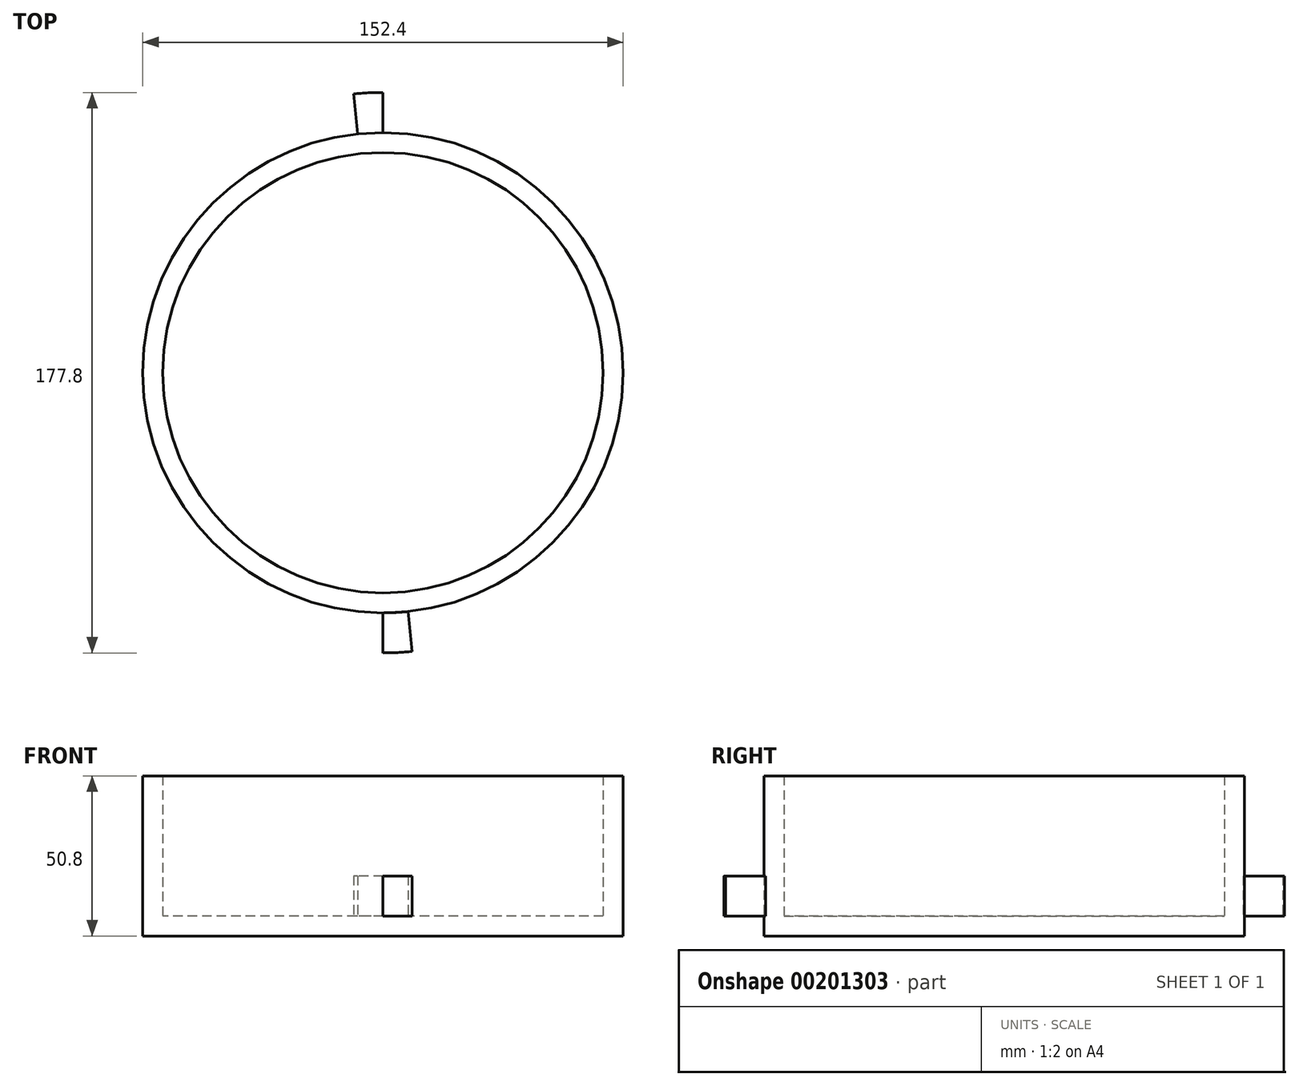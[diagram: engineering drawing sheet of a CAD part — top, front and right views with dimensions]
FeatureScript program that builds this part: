
annotation { "Feature Type Name" : "Feature", "Feature Type Description" : "" }
export const myFeature = defineFeature(function(context is Context, id is Id, definition is map)
    precondition{}
    {
        {
            var Q0;
            Q0=qCreatedBy(makeId("Top.planeOp"),FACE);
            var sketch = newSketch(context, id + "F0", { "sketchPlane" : qUnion([Q0])});
            skCircle(sketch, "E0", {"center": v(0, 0) * mm, "radius": 76.2 * mm});
            skCircle(sketch, "E1", {"center": v(0, 0) * mm, "radius": 88.9 * mm});
            skLineSegment(sketch, "E2", {"start": v(0, 0) * mm, "end": v(0, 88.9) * mm});
            skLineSegment(sketch, "E3", {"start": v(0, 0) * mm, "end": v(0, -88.9) * mm});
            skLineSegment(sketch, "E4", {"start": v(0, 0) * mm, "end": v(-9.3, 88.41) * mm});
            skLineSegment(sketch, "E5", {"start": v(0, 0) * mm, "end": v(9.3, -88.41) * mm});
            skCircle(sketch, "E6", {"center": v(0, 0) * mm, "radius": 69.85 * mm});
            skSolve(sketch);
        }
        {
            var Q0;
            {var subQ0=sQuery(id+"F0.wireOp",EDGE,"E4");var subQ1=sQuery(id+"F0.wireOp",EDGE,"E0");var subQ2=makeQuery(id+"F0.imprint","INTERSECT",VERTEX,{"derivedFrom":[subQ1,subQ0]});Q0=makeQuery(id+"F0.imprint","IMPRINT",FACE,{"disambiguationData":[TD([[makeQuery(id+"F0.imprint","IMPRINT",EDGE,{"disambiguationData":[TD([[subQ2,-1.0]])],"derivedFrom":subQ1}),1.0]])]});}
            var Q1;
            {var subQ0=sQuery(id+"F0.wireOp",EDGE,"E4");var subQ1=sQuery(id+"F0.wireOp",EDGE,"E0");var subQ2=makeQuery(id+"F0.imprint","INTERSECT",VERTEX,{"derivedFrom":[subQ1,subQ0]});Q1=makeQuery(id+"F0.imprint","IMPRINT",FACE,{"disambiguationData":[TD([[makeQuery(id+"F0.imprint","IMPRINT",EDGE,{"disambiguationData":[TD([[subQ2,1.0]])],"derivedFrom":subQ1}),1.0]])]});}
            var Q2;
            {var subQ0=sQuery(id+"F0.wireOp",EDGE,"E3");var subQ1=sQuery(id+"F0.wireOp",EDGE,"E0");var subQ2=makeQuery(id+"F0.imprint","INTERSECT",VERTEX,{"derivedFrom":[subQ1,subQ0]});Q2=makeQuery(id+"F0.imprint","IMPRINT",FACE,{"disambiguationData":[TD([[makeQuery(id+"F0.imprint","IMPRINT",EDGE,{"disambiguationData":[TD([[subQ2,-1.0]])],"derivedFrom":subQ1}),1.0]])]});}
            var Q3;
            {var subQ0=sQuery(id+"F0.wireOp",EDGE,"E2");var subQ1=sQuery(id+"F0.wireOp",EDGE,"E0");var subQ2=makeQuery(id+"F0.imprint","INTERSECT",VERTEX,{"derivedFrom":[subQ1,subQ0]});Q3=makeQuery(id+"F0.imprint","IMPRINT",FACE,{"disambiguationData":[TD([[makeQuery(id+"F0.imprint","IMPRINT",EDGE,{"disambiguationData":[TD([[subQ2,1.0]])],"derivedFrom":subQ1}),1.0]])]});}
            extrude(context, id + "F1", {"entities" : qUnion([Q0, Q1, Q2, Q3]), "depth" : 50.8 * mm});
        }
        {
            var Q0;
            {var subQ0=sQuery(id+"F0.wireOp",EDGE,"E4");var subQ1=sQuery(id+"F0.wireOp",EDGE,"E0");var subQ2=makeQuery(id+"F0.imprint","INTERSECT",VERTEX,{"derivedFrom":[subQ1,subQ0]});Q0=makeQuery(id+"F0.imprint","IMPRINT",FACE,{"disambiguationData":[TD([[makeQuery(id+"F0.imprint","IMPRINT",EDGE,{"disambiguationData":[TD([[subQ2,1.0]])],"derivedFrom":subQ1}),-1.0]])]});}
            var Q1;
            {var subQ0=sQuery(id+"F0.wireOp",EDGE,"E3");var subQ1=sQuery(id+"F0.wireOp",EDGE,"E0");var subQ2=makeQuery(id+"F0.imprint","INTERSECT",VERTEX,{"derivedFrom":[subQ1,subQ0]});Q1=makeQuery(id+"F0.imprint","IMPRINT",FACE,{"disambiguationData":[TD([[makeQuery(id+"F0.imprint","IMPRINT",EDGE,{"disambiguationData":[TD([[subQ2,-1.0]])],"derivedFrom":subQ1}),-1.0]])]});}
            extrude(context, id + "F2", {"entities" : qUnion([Q0, Q1]), "operationType" : NewBodyOperationType.ADD, "depth" : 19.05 * mm});
        }
        {
            var Q0;
            {var subQ0=sQuery(id+"F0.wireOp",EDGE,"E3");var subQ1=sQuery(id+"F0.wireOp",EDGE,"E0");var subQ2=makeQuery(id+"F0.imprint","INTERSECT",VERTEX,{"derivedFrom":[subQ1,subQ0]});Q0=makeQuery(id+"F0.imprint","IMPRINT",FACE,{"disambiguationData":[TD([[makeQuery(id+"F0.imprint","IMPRINT",EDGE,{"disambiguationData":[TD([[subQ2,-1.0]])],"derivedFrom":subQ1}),-1.0]])]});}
            var Q1;
            {var subQ0=sQuery(id+"F0.wireOp",EDGE,"E4");var subQ1=sQuery(id+"F0.wireOp",EDGE,"E0");var subQ2=makeQuery(id+"F0.imprint","INTERSECT",VERTEX,{"derivedFrom":[subQ1,subQ0]});Q1=makeQuery(id+"F0.imprint","IMPRINT",FACE,{"disambiguationData":[TD([[makeQuery(id+"F0.imprint","IMPRINT",EDGE,{"disambiguationData":[TD([[subQ2,1.0]])],"derivedFrom":subQ1}),-1.0]])]});}
            extrude(context, id + "F3", {"entities" : qUnion([Q0, Q1]), "operationType" : NewBodyOperationType.REMOVE, "depth" : 6.35 * mm});
        }
        {
            var Q0;
            {var subQ1=sQuery(id+"F0.wireOp",EDGE,"E3");var subQ3=sQuery(id+"F0.wireOp",EDGE,"E6");var subQ4=makeQuery(id+"F0.imprint","INTERSECT",VERTEX,{"derivedFrom":[subQ1,subQ3]});Q0=makeQuery(id+"F0.imprint","IMPRINT",FACE,{"disambiguationData":[TD([[makeQuery(id+"F0.imprint","IMPRINT",EDGE,{"disambiguationData":[TD([[subQ4,1.0]])],"derivedFrom":subQ3}),1.0]])]});}
            var Q1;
            {var subQ1=sQuery(id+"F0.wireOp",EDGE,"E2");var subQ3=sQuery(id+"F0.wireOp",EDGE,"E6");var subQ4=makeQuery(id+"F0.imprint","INTERSECT",VERTEX,{"derivedFrom":[subQ1,subQ3]});Q1=makeQuery(id+"F0.imprint","IMPRINT",FACE,{"disambiguationData":[TD([[makeQuery(id+"F0.imprint","IMPRINT",EDGE,{"disambiguationData":[TD([[subQ4,-1.0]])],"derivedFrom":subQ3}),1.0]])]});}
            var Q2;
            {var subQ1=sQuery(id+"F0.wireOp",EDGE,"E2");var subQ3=sQuery(id+"F0.wireOp",EDGE,"E6");var subQ4=makeQuery(id+"F0.imprint","INTERSECT",VERTEX,{"derivedFrom":[subQ1,subQ3]});Q2=makeQuery(id+"F0.imprint","IMPRINT",FACE,{"disambiguationData":[TD([[makeQuery(id+"F0.imprint","IMPRINT",EDGE,{"disambiguationData":[TD([[subQ4,1.0]])],"derivedFrom":subQ3}),1.0]])]});}
            var Q3;
            {var subQ1=sQuery(id+"F0.wireOp",EDGE,"E3");var subQ3=sQuery(id+"F0.wireOp",EDGE,"E6");var subQ4=makeQuery(id+"F0.imprint","INTERSECT",VERTEX,{"derivedFrom":[subQ1,subQ3]});Q3=makeQuery(id+"F0.imprint","IMPRINT",FACE,{"disambiguationData":[TD([[makeQuery(id+"F0.imprint","IMPRINT",EDGE,{"disambiguationData":[TD([[subQ4,-1.0]])],"derivedFrom":subQ3}),1.0]])]});}
            extrude(context, id + "F4", {"entities" : qUnion([Q0, Q1, Q2, Q3]), "operationType" : NewBodyOperationType.ADD, "depth" : 6.35 * mm});
        }
    });
